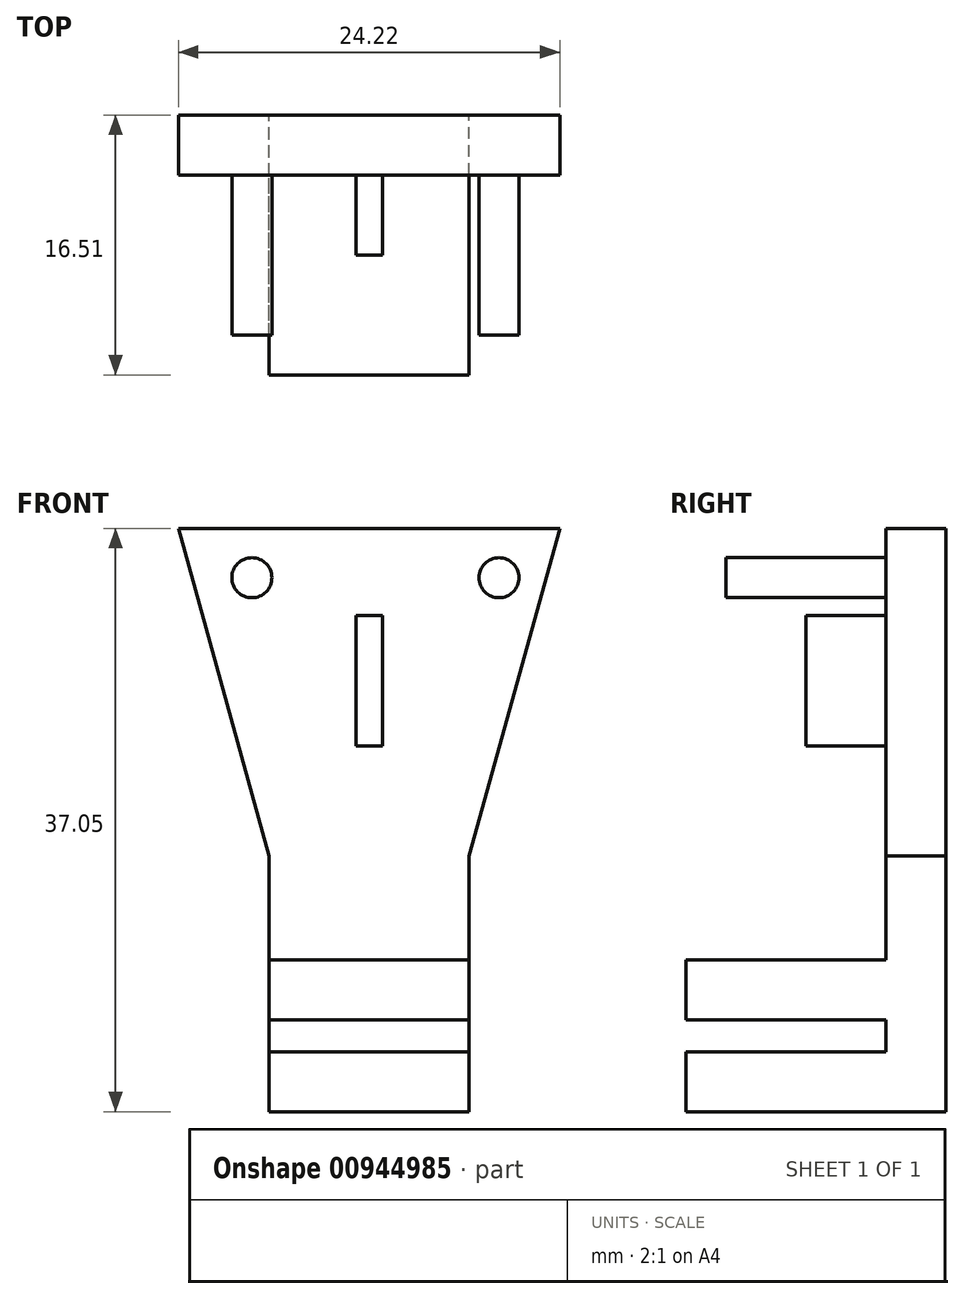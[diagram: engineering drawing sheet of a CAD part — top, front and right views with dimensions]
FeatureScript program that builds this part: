
annotation { "Feature Type Name" : "Feature", "Feature Type Description" : "" }
export const myFeature = defineFeature(function(context is Context, id is Id, definition is map)
    precondition{}
    {
        {
            var Q0;
            Q0=qCreatedBy(makeId("Front.planeOp"),FACE);
            var sketch = newSketch(context, id + "F0", { "sketchPlane" : qUnion([Q0])});
            skLineSegment(sketch, "E0.bottom", {"start": v(0, 0) * mm, "end": v(12.7, 0) * mm});
            skLineSegment(sketch, "E0.top", {"start": v(0, 16.24) * mm, "end": v(12.7, 16.24) * mm});
            skLineSegment(sketch, "E0.left", {"start": v(0, 0) * mm, "end": v(0, 16.24) * mm});
            skLineSegment(sketch, "E0.right", {"start": v(12.7, 0) * mm, "end": v(12.7, 16.24) * mm});
            skLineSegment(sketch, "E1", {"start": v(12.7, 16.24) * mm, "end": v(18.46, 37.05) * mm});
            skLineSegment(sketch, "E2", {"start": v(18.46, 37.05) * mm, "end": v(-5.76, 37.05) * mm});
            skLineSegment(sketch, "E3", {"start": v(-5.76, 37.05) * mm, "end": v(0, 16.24) * mm});
            skSolve(sketch);
        }
        {
            var Q0;
            Q0 = qSketchRegion(id + "F0", true);
            extrude(context, id + "F1", {"entities" : qUnion([Q0]), "depth" : 3.8 * mm, "offsetDistance" : 25.4 * mm});
        }
        {
            var Q0;
            Q0=makeQuery(id+"F1.opExtrude","CAP_FACE",FACE,{"disambiguationData":[OSD([sQuery(id+"F0.wireOp",EDGE,"E0.bottom"),sQuery(id+"F0.wireOp",EDGE,"E0.left"),sQuery(id+"F0.wireOp",EDGE,"E0.right"),sQuery(id+"F0.wireOp",EDGE,"E1"),sQuery(id+"F0.wireOp",EDGE,"E2"),sQuery(id+"F0.wireOp",EDGE,"E3")])],"isStart":false});
            var sketch = newSketch(context, id + "F2", { "sketchPlane" : qUnion([Q0])});
            skLineSegment(sketch, "E4.bottom", {"start": v(0, 0) * mm, "end": v(12.7, 0) * mm});
            skLineSegment(sketch, "E4.top", {"start": v(0, 3.8) * mm, "end": v(12.7, 3.8) * mm});
            skLineSegment(sketch, "E4.left", {"start": v(0, 0) * mm, "end": v(0, 3.8) * mm});
            skLineSegment(sketch, "E4.right", {"start": v(12.7, 0) * mm, "end": v(12.7, 3.8) * mm});
            skLineSegment(sketch, "E5.bottom", {"start": v(0, 5.84) * mm, "end": v(12.7, 5.84) * mm});
            skLineSegment(sketch, "E5.top", {"start": v(0, 9.65) * mm, "end": v(12.7, 9.65) * mm});
            skLineSegment(sketch, "E5.left", {"start": v(0, 5.84) * mm, "end": v(0, 9.65) * mm});
            skLineSegment(sketch, "E5.right", {"start": v(12.7, 5.84) * mm, "end": v(12.7, 9.65) * mm});
            skSolve(sketch);
        }
        {
            var Q0;
            Q0 = qSketchRegion(id + "F2", true);
            extrude(context, id + "F3", {"entities" : qUnion([Q0]), "operationType" : NewBodyOperationType.ADD, "depth" : 12.7 * mm, "offsetDistance" : 25.4 * mm});
        }
        {
            var Q0;
            {var subQ0=sQuery(id+"F0.wireOp",EDGE,"E2");var subQ1=sQuery(id+"F0.wireOp",EDGE,"E1");var subQ2=sQuery(id+"F0.wireOp",EDGE,"E0.right");var subQ3=sQuery(id+"F0.wireOp",EDGE,"E0.left");var subQ4=sQuery(id+"F0.wireOp",EDGE,"E3");Q0=makeQuery(id+"F3.boolean.opBoolean","SPLIT",FACE,{"disambiguationData":[TD([makeQuery(id+"F1.opExtrude","SWEPT_FACE",FACE,{"disambiguationData":[OSD([subQ1])]})])],"derivedFrom":makeQuery(id+"F1.opExtrude","CAP_FACE",FACE,{"disambiguationData":[OSD([sQuery(id+"F0.wireOp",EDGE,"E0.bottom"),subQ3,subQ2,subQ1,subQ0,subQ4])],"isStart":false})});}
            var sketch = newSketch(context, id + "F4", { "sketchPlane" : qUnion([Q0])});
            skCircle(sketch, "E6", {"center": v(14.6, 33.92) * mm, "radius": 1.27 * mm});
            skCircle(sketch, "E7", {"center": v(-1.1, 33.92) * mm, "radius": 1.27 * mm});
            skSolve(sketch);
        }
        {
            var Q0;
            Q0 = qSketchRegion(id + "F4", true);
            extrude(context, id + "F5", {"entities" : qUnion([Q0]), "operationType" : NewBodyOperationType.ADD, "depth" : 10.16 * mm, "offsetDistance" : 25.4 * mm});
        }
        {
            var Q0;
            {var subQ0=sQuery(id+"F0.wireOp",EDGE,"E2");var subQ1=sQuery(id+"F0.wireOp",EDGE,"E1");var subQ2=sQuery(id+"F0.wireOp",EDGE,"E0.right");var subQ3=sQuery(id+"F0.wireOp",EDGE,"E0.left");var subQ4=sQuery(id+"F0.wireOp",EDGE,"E3");Q0=makeQuery(id+"F3.boolean.opBoolean","SPLIT",FACE,{"disambiguationData":[TD([makeQuery(id+"F1.opExtrude","SWEPT_FACE",FACE,{"disambiguationData":[OSD([subQ1])]})])],"derivedFrom":makeQuery(id+"F1.opExtrude","CAP_FACE",FACE,{"disambiguationData":[OSD([sQuery(id+"F0.wireOp",EDGE,"E0.bottom"),subQ3,subQ2,subQ1,subQ0,subQ4])],"isStart":false})});}
            var sketch = newSketch(context, id + "F6", { "sketchPlane" : qUnion([Q0])});
            skLineSegment(sketch, "E8.bottom", {"start": v(5.5, 31.52) * mm, "end": v(7.2, 31.52) * mm});
            skLineSegment(sketch, "E8.top", {"start": v(5.5, 23.23) * mm, "end": v(7.2, 23.23) * mm});
            skLineSegment(sketch, "E8.left", {"start": v(5.5, 31.52) * mm, "end": v(5.5, 23.23) * mm});
            skLineSegment(sketch, "E8.right", {"start": v(7.2, 31.52) * mm, "end": v(7.2, 23.23) * mm});
            skSolve(sketch);
        }
        {
            var Q0;
            Q0 = qSketchRegion(id + "F6", true);
            extrude(context, id + "F7", {"entities" : qUnion([Q0]), "operationType" : NewBodyOperationType.ADD, "depth" : 5.08 * mm, "offsetDistance" : 25.4 * mm});
        }
    });
